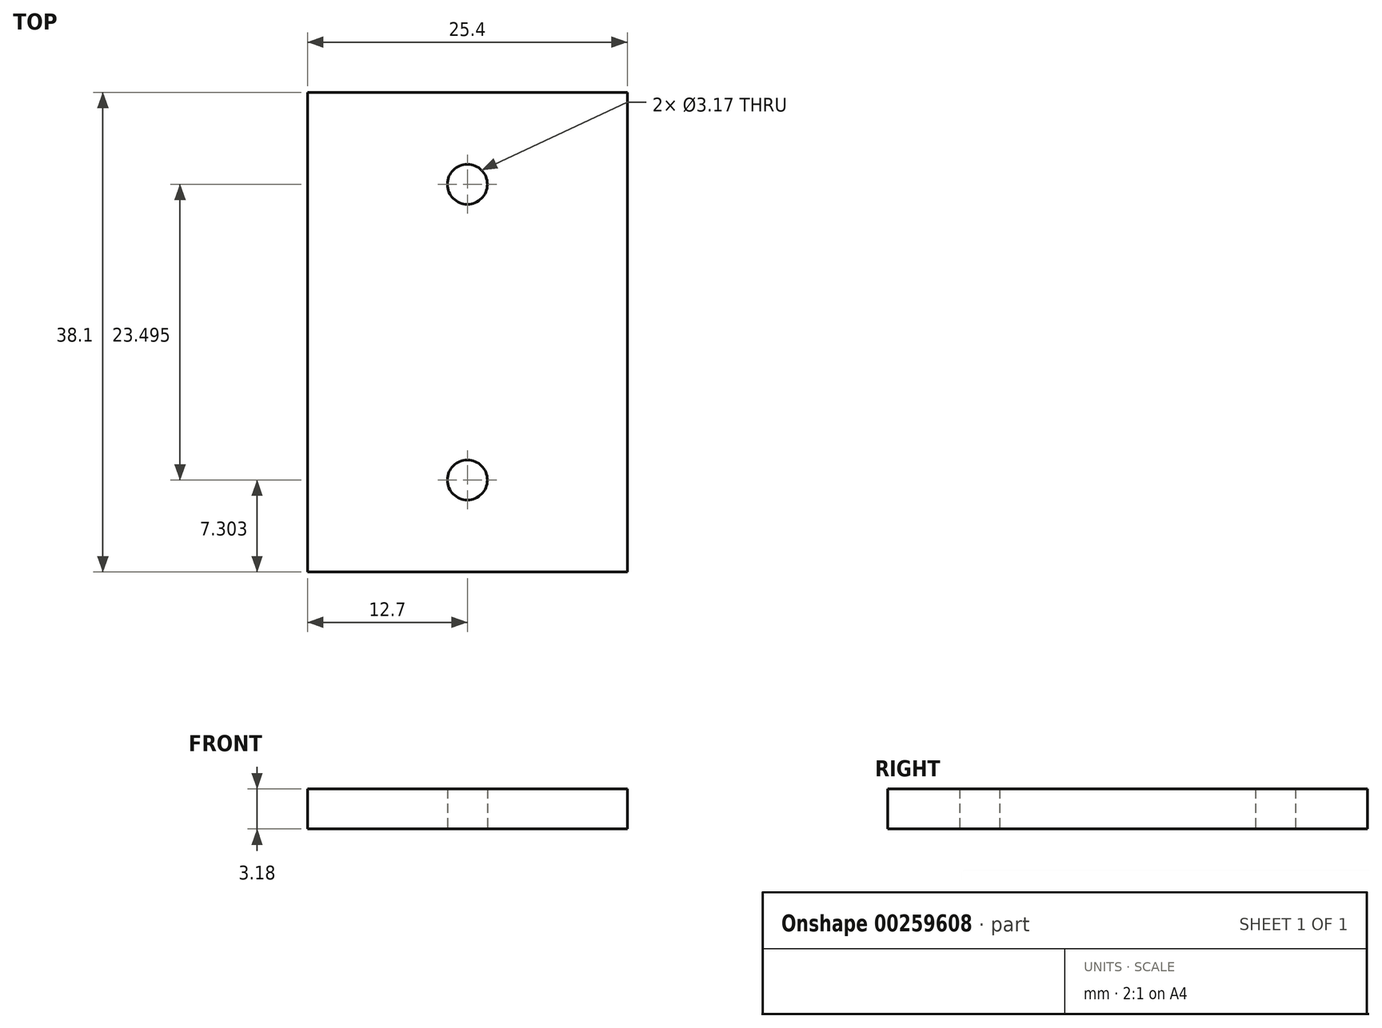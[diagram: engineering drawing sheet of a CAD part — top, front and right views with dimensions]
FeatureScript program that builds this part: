
annotation { "Feature Type Name" : "Feature", "Feature Type Description" : "" }
export const myFeature = defineFeature(function(context is Context, id is Id, definition is map)
    precondition{}
    {
        {
            var Q0;
            Q0=qCreatedBy(makeId("Top.planeOp"),FACE);
            var sketch = newSketch(context, id + "F0", { "sketchPlane" : qUnion([Q0])});
            skLineSegment(sketch, "E0.bottom", {"start": v(-12.7, 19.05) * mm, "end": v(12.7, 19.05) * mm});
            skLineSegment(sketch, "E0.top", {"start": v(-12.7, -19.05) * mm, "end": v(12.7, -19.05) * mm});
            skLineSegment(sketch, "E0.left", {"start": v(-12.7, 19.05) * mm, "end": v(-12.7, -19.05) * mm});
            skLineSegment(sketch, "E0.right", {"start": v(12.7, 19.05) * mm, "end": v(12.7, -19.05) * mm});
            skPoint(sketch, "E0.middle", {"position": v(0, 0) * mm});
            skCircle(sketch, "E1", {"center": v(0, 11.75) * mm, "radius": 1.59 * mm});
            skCircle(sketch, "E2", {"center": v(0, -11.75) * mm, "radius": 1.59 * mm});
            skSolve(sketch);
        }
        {
            var Q0;
            Q0=makeQuery(id+"F0.imprint","IMPRINT",FACE,{"disambiguationData":[TD([[makeQuery(id+"F0.imprint","IMPRINT",EDGE,{"derivedFrom":sQuery(id+"F0.wireOp",EDGE,"E0.bottom")}),-1.0]])]});
            extrude(context, id + "F1", {"entities" : qUnion([Q0]), "depth" : 3.17 * mm});
        }
    });
